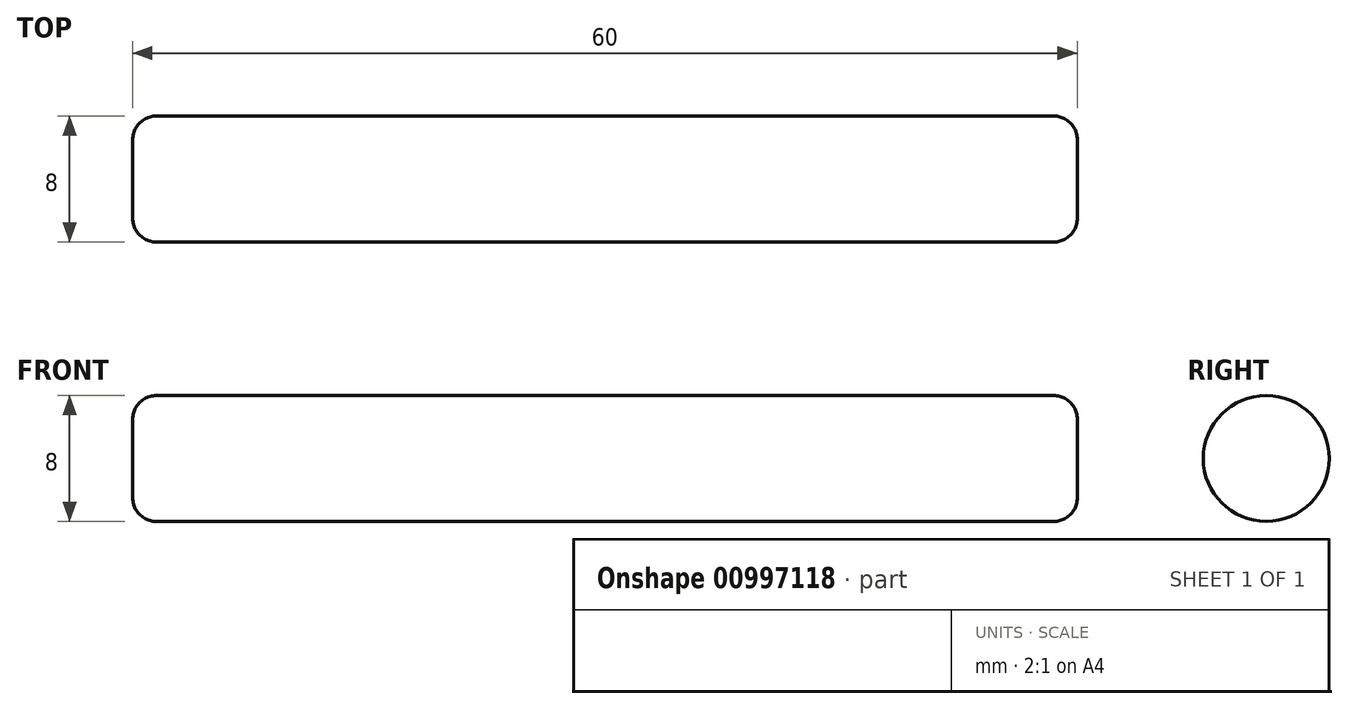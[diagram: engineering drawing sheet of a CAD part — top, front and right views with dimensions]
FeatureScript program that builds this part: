
annotation { "Feature Type Name" : "Feature", "Feature Type Description" : "" }
export const myFeature = defineFeature(function(context is Context, id is Id, definition is map)
    precondition{}
    {
        {
            var Q0;
            Q0=qCreatedBy(makeId("Front.planeOp"),FACE);
            var sketch = newSketch(context, id + "F0", { "sketchPlane" : qUnion([Q0])});
            skLineSegment(sketch, "E0", {"start": v(-30, 0) * mm, "end": v(30, 0) * mm});
            skLineSegment(sketch, "E1", {"start": v(30, 0) * mm, "end": v(30, 2.5) * mm});
            skLineSegment(sketch, "E2", {"start": v(-30, 0) * mm, "end": v(-30, 2.5) * mm});
            skArc(sketch, "E3", {"start": v(-30, 2.5) * mm, "mid": v(-29.56, 3.56) * mm, "end": v(-28.5, 4) * mm});
            skArc(sketch, "E4", {"start": v(30, 2.5) * mm, "mid": v(29.56, 3.56) * mm, "end": v(28.5, 4) * mm});
            skLineSegment(sketch, "E5", {"start": v(-28.5, 4) * mm, "end": v(28.5, 4) * mm});
            skSolve(sketch);
        }
        {
            var Q0;
            Q0 = qSketchRegion(id + "F0", true);
            var Q1;
            Q1=sQuery(id+"F0.wireOp",EDGE,"E0");
            revolve(context, id + "F1", {"surfaceOperationType" : NewSurfaceOperationType.NEW, "entities" : qUnion([Q0]), "axis" : qUnion([Q1]), "revolveType" : RevolveType.FULL});
        }
    });
